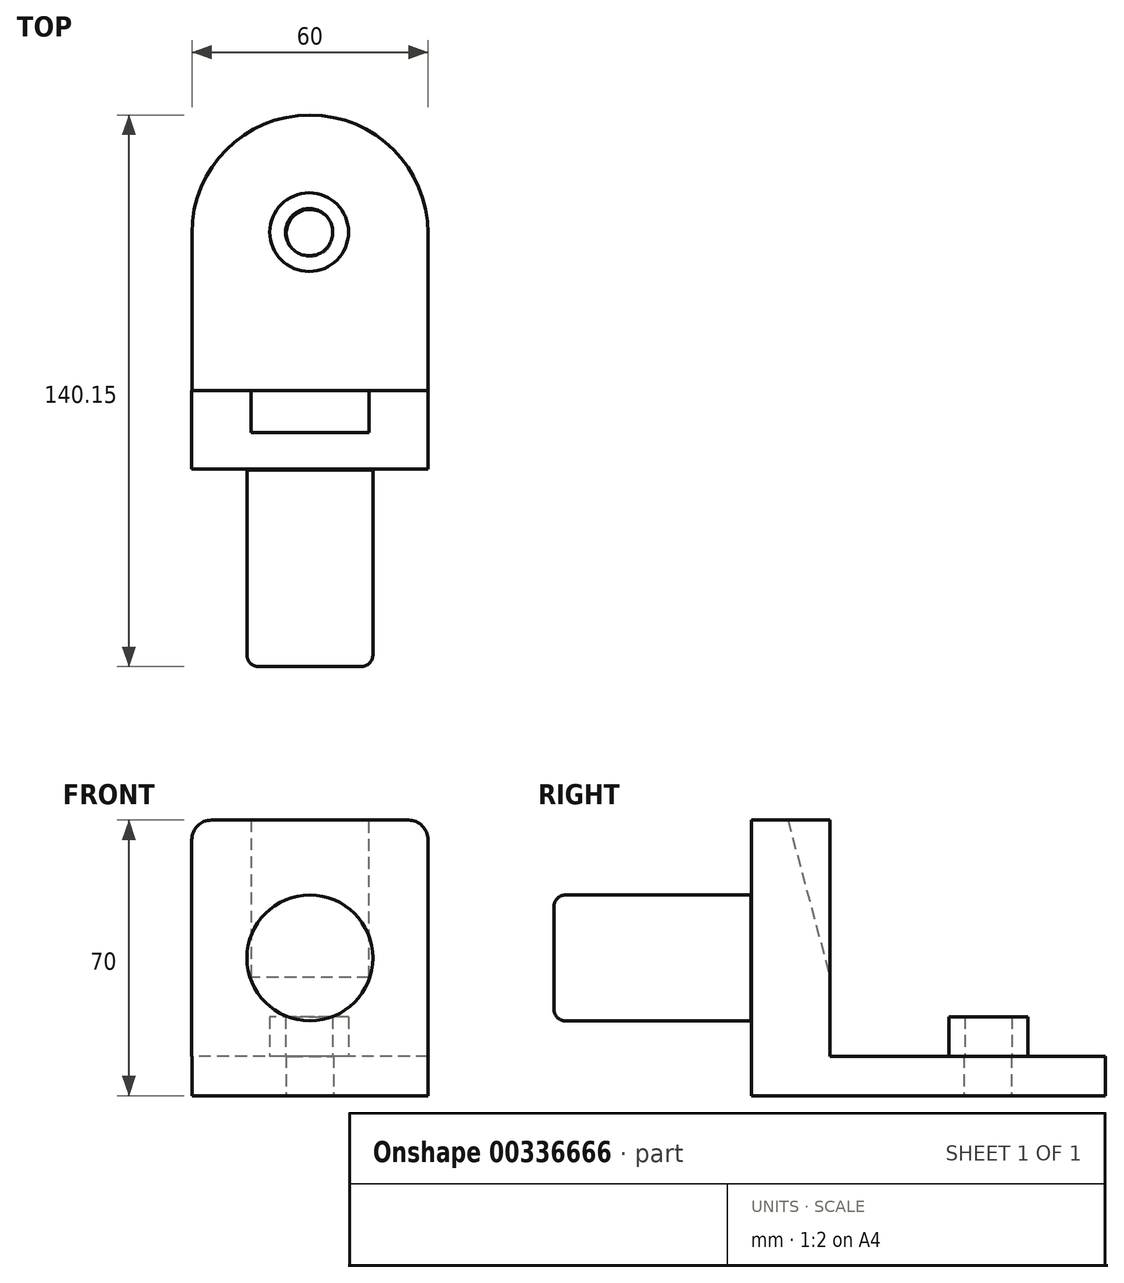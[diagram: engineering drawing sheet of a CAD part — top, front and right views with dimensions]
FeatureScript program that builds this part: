
annotation { "Feature Type Name" : "Feature", "Feature Type Description" : "" }
export const myFeature = defineFeature(function(context is Context, id is Id, definition is map)
    precondition{}
    {
        {
            var Q0;
            Q0=qCreatedBy(makeId("Top.planeOp"),FACE);
            var sketch = newSketch(context, id + "F0", { "sketchPlane" : qUnion([Q0])});
            skLineSegment(sketch, "E0", {"start": v(7.42, 30.95) * mm, "end": v(7.42, 30.95) * mm});
            skLineSegment(sketch, "E1", {"start": v(37.42, 0.95) * mm, "end": v(37.42, -59.05) * mm});
            skLineSegment(sketch, "E2", {"start": v(37.42, -59.05) * mm, "end": v(-22.58, -59.05) * mm});
            skLineSegment(sketch, "E3", {"start": v(-22.58, -59.05) * mm, "end": v(-22.58, 0.95) * mm});
            skPoint(sketch, "E4.visualSharp", {"position": v(-22.58, 30.95) * mm});
            skArc(sketch, "E4.filletArc", {"start": v(7.42, 30.95) * mm, "mid": v(-13.8, 22.17) * mm, "end": v(-22.58, 0.95) * mm});
            skPoint(sketch, "E5.visualSharp", {"position": v(37.42, 30.95) * mm});
            skArc(sketch, "E5.filletArc", {"start": v(37.42, 0.95) * mm, "mid": v(28.63, 22.17) * mm, "end": v(7.42, 30.95) * mm});
            skCircle(sketch, "E6", {"center": v(7.42, 0.95) * mm, "radius": 6 * mm});
            skSolve(sketch);
        }
        {
            var Q0;
            Q0=qCreatedBy(makeId("Top.planeOp"),FACE);
            cPlane(context, id + "F1", {"entities" : qUnion([Q0]), "cplaneType" : CPlaneType.OFFSET, "offset" : 10 * mm, "width" : 150 * mm, "height" : 150 * mm});
        }
        {
            var Q0;
            Q0=qCreatedBy(id+"F1.planeOp",FACE);
            var sketch = newSketch(context, id + "F2", { "sketchPlane" : qUnion([Q0])});
            skPoint(sketch, "E7.end.orphan", {"position": v(9.03, 1.2) * mm});
            skPoint(sketch, "E8.orphan", {"position": v(37.23, 1.2) * mm});
            skCircle(sketch, "E9", {"center": v(7.23, 1.2) * mm, "radius": 6 * mm});
            skCircle(sketch, "E10", {"center": v(7.23, 1.2) * mm, "radius": 10 * mm});
            skPoint(sketch, "E11.orphan", {"position": v(-22.77, 1.2) * mm});
            skSolve(sketch);
        }
        {
            var Q0;
            Q0=makeQuery(id+"F0.imprint","IMPRINT",FACE,{"disambiguationData":[TD([[makeQuery(id+"F0.imprint","IMPRINT",EDGE,{"derivedFrom":sQuery(id+"F0.wireOp",EDGE,"E1")}),-1.0]])]});
            extrude(context, id + "F3", {"entities" : qUnion([Q0]), "depth" : 10 * mm});
        }
        {
            var Q0;
            Q0=makeQuery(id+"F2.imprint","IMPRINT",FACE,{"disambiguationData":[TD([[makeQuery(id+"F2.imprint","IMPRINT",EDGE,{"derivedFrom":sQuery(id+"F2.wireOp",EDGE,"E9")}),-1.0]])]});
            extrude(context, id + "F4", {"entities" : qUnion([Q0]), "operationType" : NewBodyOperationType.ADD, "depth" : 10 * mm});
        }
        {
            var Q0;
            Q0=qCreatedBy(id+"F1.planeOp",FACE);
            var sketch = newSketch(context, id + "F5", { "sketchPlane" : qUnion([Q0])});
            skLineSegment(sketch, "E12", {"start": v(-22.58, -59.04) * mm, "end": v(-22.58, -39.04) * mm});
            skPoint(sketch, "E13.end.orphan", {"position": v(37.43, -59.04) * mm});
            skPoint(sketch, "E14.start.orphan", {"position": v(-7.58, -59.04) * mm});
            skLineSegment(sketch, "E15", {"start": v(-22.58, -59.04) * mm, "end": v(37.42, -59.04) * mm});
            skLineSegment(sketch, "E16", {"start": v(37.42, -59.04) * mm, "end": v(37.42, -39.04) * mm});
            skLineSegment(sketch, "E17", {"start": v(37.42, -39.04) * mm, "end": v(-22.58, -39.04) * mm});
            skSolve(sketch);
        }
        {
            var Q0;
            Q0=makeQuery(id+"F5.imprint","IMPRINT",FACE,{"disambiguationData":[TD([[makeQuery(id+"F5.imprint","IMPRINT",EDGE,{"derivedFrom":sQuery(id+"F5.wireOp",EDGE,"E12")}),-1.0]])]});
            var Q1;
            Q1=makeQuery(id+"F5.imprint","IMPRINT",FACE,{"disambiguationData":[TD([[makeQuery(id+"F5.imprint","IMPRINT",EDGE,{"derivedFrom":sQuery(id+"F5.wireOp",EDGE,"OVBsP2zE-rVl6-sqWZ-EnEW-24gt2Fn9uIpZ")}),1.0]])]});
            extrude(context, id + "F6", {"entities" : qUnion([Q0, Q1]), "operationType" : NewBodyOperationType.ADD, "depth" : 60 * mm});
        }
        {
            var Q0;
            Q0 = qSketchRegion(id + "F5", true);
            extrude(context, id + "F7", {"entities" : qUnion([Q0]), "operationType" : NewBodyOperationType.ADD, "depth" : 60 * mm});
        }
        {
            var Q0;
            Q0=qCreatedBy(makeId("Front.planeOp"),FACE);
            cPlane(context, id + "F8", {"entities" : qUnion([Q0]), "cplaneType" : CPlaneType.OFFSET, "offset" : 59.2 * mm, "width" : 150 * mm, "height" : 150 * mm});
        }
        {
            var Q0;
            Q0=qCreatedBy(id+"F8.planeOp",FACE);
            var sketch = newSketch(context, id + "F9", { "sketchPlane" : qUnion([Q0])});
            skLineSegment(sketch, "E18", {"start": v(-3.43, 0) * mm, "end": v(27.73, 0) * mm});
            skPoint(sketch, "E19.start.orphan", {"position": v(-3.43, 70) * mm});
            skCircle(sketch, "E20", {"center": v(7.42, 35) * mm, "radius": 16 * mm});
            skPoint(sketch, "E21.orphan", {"position": v(-14.67, 19) * mm});
            skPoint(sketch, "E22.orphan", {"position": v(-22.58, 35) * mm});
            skPoint(sketch, "E23.end.orphan", {"position": v(-14.67, 51) * mm});
            skPoint(sketch, "E23.start.orphan", {"position": v(-14.67, 35) * mm});
            skPoint(sketch, "E24.end.orphan", {"position": v(27.73, 70) * mm});
            skPoint(sketch, "E24.start.orphan", {"position": v(27.73, 51) * mm});
            skPoint(sketch, "E25.orphan", {"position": v(37.42, 35) * mm});
            skSolve(sketch);
        }
        {
            var Q0;
            Q0=makeQuery(id+"F9.imprint","IMPRINT",FACE,{"disambiguationData":[TD([[makeQuery(id+"F9.imprint","IMPRINT",EDGE,{"derivedFrom":sQuery(id+"F9.wireOp",EDGE,"E20")}),1.0]])]});
            extrude(context, id + "F10", {"entities" : qUnion([Q0]), "depth" : 50 * mm});
        }
        {
            var Q0;
            Q0=makeQuery(id+"F10.opExtrude","CAP_EDGE",EDGE,{"disambiguationData":[OSD([sQuery(id+"F9.wireOp",EDGE,"E20")])],"isStart":false});
            fillet(context, id + "F11", {"entities" : qUnion([Q0]), "radius" : 3 * mm, "tangentPropagation" : true, "allowEdgeOverflow" : false});
        }
        {
            var Q0;
            Q0=makeQuery(id+"F6.opExtrude","SWEPT_FACE",FACE,{"disambiguationData":[OSD([sQuery(id+"F5.wireOp",EDGE,"E16")])]});
            var sketch = newSketch(context, id + "F12", { "sketchPlane" : qUnion([Q0])});
            skLineSegment(sketch, "E26", {"start": v(-39.04, 70) * mm, "end": v(-39.04, 30) * mm});
            skLineSegment(sketch, "E27", {"start": v(-39.04, 30) * mm, "end": v(-49.76, 70) * mm});
            skLineSegment(sketch, "E28", {"start": v(-49.76, 70) * mm, "end": v(-39.04, 70) * mm});
            skSolve(sketch);
        }
        {
            var Q0;
            Q0=makeQuery(id+"F6.opExtrude","SWEPT_FACE",FACE,{"disambiguationData":[OSD([sQuery(id+"F5.wireOp",EDGE,"E12")])]});
            var sketch = newSketch(context, id + "F13", { "sketchPlane" : qUnion([Q0])});
            skLineSegment(sketch, "E29", {"start": v(39.04, 70) * mm, "end": v(39.04, 30) * mm});
            skLineSegment(sketch, "E30", {"start": v(39.04, 30) * mm, "end": v(49.76, 70) * mm});
            skLineSegment(sketch, "E31", {"start": v(39.04, 70) * mm, "end": v(49.76, 70) * mm});
            skSolve(sketch);
        }
        {
            var Q0;
            Q0 = qSketchRegion(id + "F13", true);
            extrude(context, id + "F14", {"entities" : qUnion([Q0]), "operationType" : NewBodyOperationType.REMOVE, "oppositeDirection" : true, "depth" : 68.3 * mm});
        }
        {
            var Q0;
            Q0=makeQuery(id+"F12.imprint","IMPRINT",FACE,{"disambiguationData":[TD([[makeQuery(id+"F12.imprint","IMPRINT",EDGE,{"derivedFrom":sQuery(id+"F12.wireOp",EDGE,"E26")}),-1.0]])]});
            var Q1;
            {var subQ3=sQuery(id+"F12.wireOp",EDGE,"E27");Q1=makeQuery(id+"F12.imprint","IMPRINT",FACE,{"disambiguationData":[TD([[makeQuery(id+"F12.imprint","IMPRINT",EDGE,{"derivedFrom":subQ3}),1.0]])]});}
            extrude(context, id + "F15", {"entities" : qUnion([Q0, Q1]), "operationType" : NewBodyOperationType.ADD, "oppositeDirection" : true, "depth" : 15 * mm});
        }
        {
            var Q0;
            Q0=makeQuery(id+"F13.imprint","IMPRINT",FACE,{"disambiguationData":[TD([[makeQuery(id+"F13.imprint","IMPRINT",EDGE,{"derivedFrom":sQuery(id+"F13.wireOp",EDGE,"E29")}),1.0]])]});
            var Q1;
            {var subQ3=sQuery(id+"F13.wireOp",EDGE,"E30");Q1=makeQuery(id+"F13.imprint","IMPRINT",FACE,{"disambiguationData":[TD([[makeQuery(id+"F13.imprint","IMPRINT",EDGE,{"derivedFrom":subQ3}),-1.0]])]});}
            extrude(context, id + "F16", {"entities" : qUnion([Q0, Q1]), "operationType" : NewBodyOperationType.ADD, "oppositeDirection" : true, "depth" : 15 * mm});
        }
        {
            var Q0;
            {var subQ0=sQuery(id+"F5.wireOp",EDGE,"E16");Q0=makeQuery(id+"F15.boolean.opBoolean","MERGE",EDGE,{"derivedFrom":[makeQuery(id+"F6.opExtrude","CAP_EDGE",EDGE,{"disambiguationData":[OSD([subQ0])],"isStart":false}),makeQuery(id+"F15.opExtrude","CAP_EDGE",EDGE,{"disambiguationData":[OSD([subQ0,sQuery(id+"F12.wireOp",EDGE,"E28")])],"isStart":true})]});}
            var Q1;
            {var subQ0=sQuery(id+"F5.wireOp",EDGE,"E12");Q1=makeQuery(id+"F16.boolean.opBoolean","MERGE",EDGE,{"derivedFrom":[makeQuery(id+"F6.opExtrude","CAP_EDGE",EDGE,{"disambiguationData":[OSD([subQ0])],"isStart":false}),makeQuery(id+"F16.opExtrude","CAP_EDGE",EDGE,{"disambiguationData":[OSD([subQ0,sQuery(id+"F13.wireOp",EDGE,"E31")])],"isStart":true})]});}
            fillet(context, id + "F17", {"entities" : qUnion([Q0, Q1]), "radius" : 5 * mm, "tangentPropagation" : true, "allowEdgeOverflow" : false});
        }
    });
